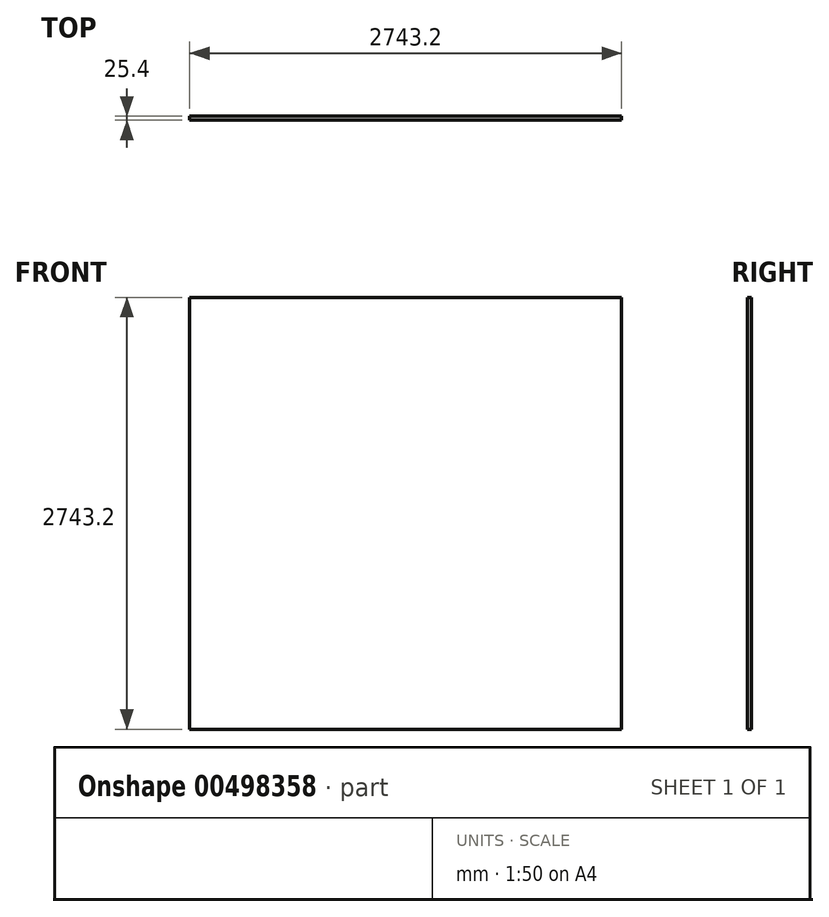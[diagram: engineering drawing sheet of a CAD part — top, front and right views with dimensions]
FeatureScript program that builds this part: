
annotation { "Feature Type Name" : "Feature", "Feature Type Description" : "" }
export const myFeature = defineFeature(function(context is Context, id is Id, definition is map)
    precondition{}
    {
        {
            var Q0;
            Q0=qCreatedBy(makeId("Front.planeOp"),FACE);
            var sketch = newSketch(context, id + "F0", { "sketchPlane" : qUnion([Q0])});
            skLineSegment(sketch, "E0.bottom", {"start": v(-1393.1, 1793.04) * mm, "end": v(1350.1, 1793.04) * mm});
            skLineSegment(sketch, "E0.top", {"start": v(-1393.1, -950.16) * mm, "end": v(1350.1, -950.16) * mm});
            skLineSegment(sketch, "E0.left", {"start": v(-1393.1, 1793.04) * mm, "end": v(-1393.1, -950.16) * mm});
            skLineSegment(sketch, "E0.right", {"start": v(1350.1, 1793.04) * mm, "end": v(1350.1, -950.16) * mm});
            skSolve(sketch);
        }
        {
            var Q0;
            Q0=makeQuery(id+"F0.imprint","IMPRINT",FACE,{"disambiguationData":[TD([[makeQuery(id+"F0.imprint","IMPRINT",EDGE,{"derivedFrom":sQuery(id+"F0.wireOp",EDGE,"E0.bottom")}),-1.0]])]});
            extrude(context, id + "F1", {"entities" : qUnion([Q0]), "depth" : 25.4 * mm});
        }
    });
